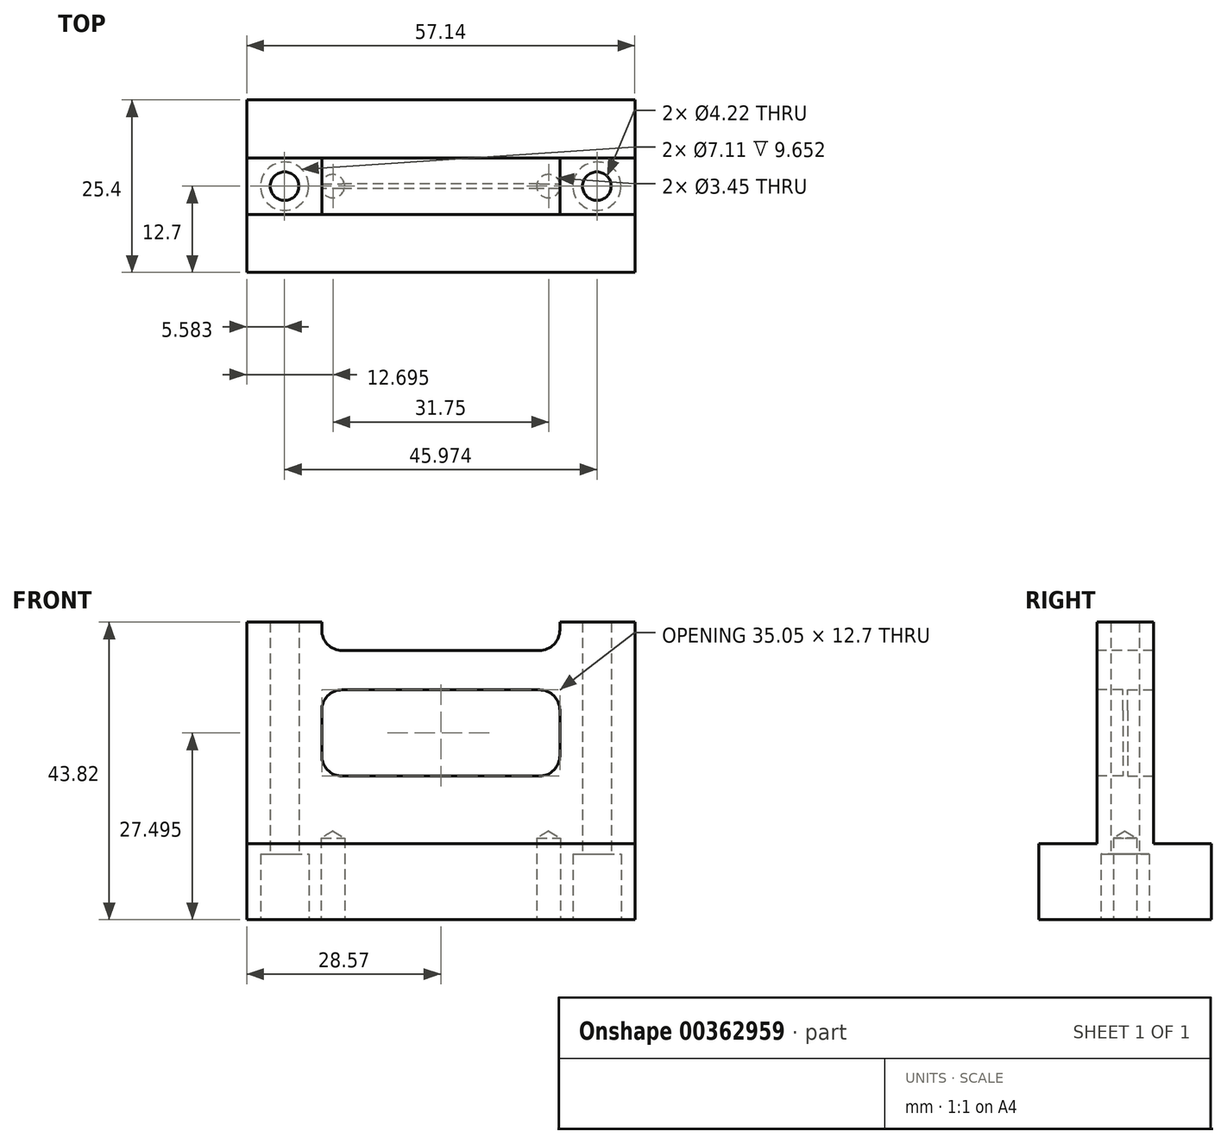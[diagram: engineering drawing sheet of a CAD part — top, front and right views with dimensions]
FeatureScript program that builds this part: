
annotation { "Feature Type Name" : "Feature", "Feature Type Description" : "" }
export const myFeature = defineFeature(function(context is Context, id is Id, definition is map)
    precondition{}
    {
        {
            var Q0;
            Q0=qCreatedBy(makeId("Top.planeOp"),FACE);
            var sketch = newSketch(context, id + "F0", { "sketchPlane" : qUnion([Q0])});
            skLineSegment(sketch, "E0.bottom", {"start": v(28.58, 12.7) * mm, "end": v(-28.58, 12.7) * mm});
            skLineSegment(sketch, "E0.top", {"start": v(28.58, -12.7) * mm, "end": v(-28.58, -12.7) * mm});
            skLineSegment(sketch, "E0.left", {"start": v(28.58, 12.7) * mm, "end": v(28.58, -12.7) * mm});
            skLineSegment(sketch, "E0.right", {"start": v(-28.58, 12.7) * mm, "end": v(-28.58, -12.7) * mm});
            skPoint(sketch, "E0.middle", {"position": v(0, 0) * mm});
            skSolve(sketch);
        }
        {
            var Q0;
            Q0=makeQuery(id+"F0.imprint","IMPRINT",FACE,{"disambiguationData":[TD([[makeQuery(id+"F0.imprint","IMPRINT",EDGE,{"derivedFrom":sQuery(id+"F0.wireOp",EDGE,"E0.bottom")}),1.0]])]});
            extrude(context, id + "F1", {"entities" : qUnion([Q0]), "depth" : 11.18 * mm});
        }
        {
            var Q0;
            Q0=makeQuery(id+"F1.opExtrude","CAP_FACE",FACE,{"disambiguationData":[OSD([sQuery(id+"F0.wireOp",EDGE,"E0.bottom"),sQuery(id+"F0.wireOp",EDGE,"E0.top"),sQuery(id+"F0.wireOp",EDGE,"E0.left"),sQuery(id+"F0.wireOp",EDGE,"E0.right")])],"isStart":false});
            var sketch = newSketch(context, id + "F2", { "sketchPlane" : qUnion([Q0])});
            skLineSegment(sketch, "E1.bottom", {"start": v(28.58, 4.15) * mm, "end": v(-28.58, 4.15) * mm});
            skLineSegment(sketch, "E1.top", {"start": v(28.58, -4.15) * mm, "end": v(-28.58, -4.15) * mm});
            skLineSegment(sketch, "E1.left", {"start": v(28.58, 4.15) * mm, "end": v(28.58, -4.15) * mm});
            skLineSegment(sketch, "E1.right", {"start": v(-28.58, 4.15) * mm, "end": v(-28.58, -4.15) * mm});
            skPoint(sketch, "E1.middle", {"position": v(0, 0) * mm});
            skSolve(sketch);
        }
        {
            var Q0;
            Q0=makeQuery(id+"F2.imprint","IMPRINT",FACE,{"disambiguationData":[TD([[makeQuery(id+"F2.imprint","IMPRINT",EDGE,{"derivedFrom":sQuery(id+"F2.wireOp",EDGE,"E1.bottom")}),1.0]])]});
            extrude(context, id + "F3", {"entities" : qUnion([Q0]), "operationType" : NewBodyOperationType.ADD, "depth" : 32.64 * mm});
        }
        {
            var Q0;
            Q0=makeQuery(id+"F3.opExtrude","SWEPT_FACE",FACE,{"disambiguationData":[OSD([sQuery(id+"F2.wireOp",EDGE,"E1.top")])]});
            var sketch = newSketch(context, id + "F4", { "sketchPlane" : qUnion([Q0])});
            skLineSegment(sketch, "E2.bottom", {"start": v(14.5, 33.85) * mm, "end": v(-14.5, 33.85) * mm});
            skLineSegment(sketch, "E2.top", {"start": v(14.5, 21.15) * mm, "end": v(-14.5, 21.15) * mm});
            skLineSegment(sketch, "E2.left", {"start": v(17.53, 30.82) * mm, "end": v(17.53, 24.17) * mm});
            skLineSegment(sketch, "E2.right", {"start": v(-17.53, 30.82) * mm, "end": v(-17.53, 24.17) * mm});
            skPoint(sketch, "E2.middle", {"position": v(0, 27.5) * mm});
            skPoint(sketch, "E2.middle.positionSnap0", {"position": v(-28.58, 27.5) * mm});
            skPoint(sketch, "E2.middle.positionSnap1", {"position": v(0, 43.82) * mm});
            skPoint(sketch, "E2.centerSnap0", {"position": v(-28.58, 27.5) * mm});
            skPoint(sketch, "E2.centerSnap1", {"position": v(0, 43.82) * mm});
            skPoint(sketch, "E3.visualSharp", {"position": v(-17.53, 33.85) * mm});
            skArc(sketch, "E3.filletArc", {"start": v(-14.5, 33.85) * mm, "mid": v(-16.64, 32.96) * mm, "end": v(-17.53, 30.82) * mm});
            skPoint(sketch, "E4.visualSharp", {"position": v(17.53, 33.85) * mm});
            skArc(sketch, "E4.filletArc", {"start": v(17.53, 30.82) * mm, "mid": v(16.64, 32.96) * mm, "end": v(14.5, 33.85) * mm});
            skPoint(sketch, "E5.visualSharp", {"position": v(17.53, 21.15) * mm});
            skArc(sketch, "E5.filletArc", {"start": v(14.5, 21.15) * mm, "mid": v(16.64, 22.03) * mm, "end": v(17.53, 24.17) * mm});
            skPoint(sketch, "E6.visualSharp", {"position": v(-17.53, 21.15) * mm});
            skArc(sketch, "E6.filletArc", {"start": v(-17.53, 24.17) * mm, "mid": v(-16.64, 22.03) * mm, "end": v(-14.5, 21.15) * mm});
            skLineSegment(sketch, "E7.bottom", {"start": v(-14.5, 39.65) * mm, "end": v(14.5, 39.65) * mm});
            skLineSegment(sketch, "E7.top", {"start": v(-17.53, 47.98) * mm, "end": v(17.53, 47.98) * mm});
            skLineSegment(sketch, "E7.left", {"start": v(-17.53, 42.67) * mm, "end": v(-17.53, 47.98) * mm});
            skLineSegment(sketch, "E7.right", {"start": v(17.53, 42.67) * mm, "end": v(17.53, 47.98) * mm});
            skPoint(sketch, "E8.visualSharp", {"position": v(-17.53, 39.65) * mm});
            skArc(sketch, "E8.filletArc", {"start": v(-17.53, 42.67) * mm, "mid": v(-16.64, 40.54) * mm, "end": v(-14.5, 39.65) * mm});
            skPoint(sketch, "E9.visualSharp", {"position": v(17.53, 39.65) * mm});
            skArc(sketch, "E9.filletArc", {"start": v(14.5, 39.65) * mm, "mid": v(16.64, 40.54) * mm, "end": v(17.53, 42.67) * mm});
            skSolve(sketch);
        }
        {
            var Q0;
            Q0=makeQuery(id+"F4.imprint","IMPRINT",FACE,{"disambiguationData":[TD([[makeQuery(id+"F4.imprint","IMPRINT",EDGE,{"derivedFrom":sQuery(id+"F4.wireOp",EDGE,"E2.bottom")}),1.0]])]});
            extrude(context, id + "F5", {"entities" : qUnion([Q0]), "operationType" : NewBodyOperationType.REMOVE, "oppositeDirection" : true, "depth" : 3.8 * mm});
        }
        {
            var Q0;
            Q0=makeQuery(id+"F4.imprint","IMPRINT",FACE,{"disambiguationData":[TD([[makeQuery(id+"F4.imprint","IMPRINT",EDGE,{"derivedFrom":sQuery(id+"F4.wireOp",EDGE,"E7.bottom")}),1.0]])]});
            extrude(context, id + "F6", {"entities" : qUnion([Q0]), "operationType" : NewBodyOperationType.REMOVE, "endBound" : BoundingType.THROUGH_ALL, "oppositeDirection" : true, "depth" : 25.4 * mm});
        }
        {
            var Q0;
            Q0=makeQuery(id+"F3.opExtrude","SWEPT_FACE",FACE,{"disambiguationData":[OSD([sQuery(id+"F2.wireOp",EDGE,"E1.bottom")])]});
            var sketch = newSketch(context, id + "F7", { "sketchPlane" : qUnion([Q0])});
            skLineSegment(sketch, "E10.0", {"start": v(-17.53, 30.82) * mm, "end": v(-17.53, 24.17) * mm});
            skPoint(sketch, "E11.0", {"position": v(-16.64, 32.96) * mm});
            skLineSegment(sketch, "E12.0", {"start": v(-14.5, 33.85) * mm, "end": v(14.5, 33.85) * mm});
            skLineSegment(sketch, "E13.0", {"start": v(17.53, 30.82) * mm, "end": v(17.53, 24.17) * mm});
            skLineSegment(sketch, "E14.0", {"start": v(-14.5, 21.15) * mm, "end": v(14.5, 21.15) * mm});
            skArc(sketch, "E15.0", {"start": v(17.53, 24.17) * mm, "mid": v(16.64, 22.03) * mm, "end": v(14.5, 21.15) * mm});
            skArc(sketch, "E16.0", {"start": v(14.5, 33.85) * mm, "mid": v(16.64, 32.96) * mm, "end": v(17.53, 30.82) * mm});
            skArc(sketch, "E17.0", {"start": v(-17.53, 30.82) * mm, "mid": v(-16.64, 32.96) * mm, "end": v(-14.5, 33.85) * mm});
            skArc(sketch, "E18.0", {"start": v(-14.5, 21.15) * mm, "mid": v(-16.64, 22.03) * mm, "end": v(-17.53, 24.17) * mm});
            skSolve(sketch);
        }
        {
            var Q0;
            Q0=makeQuery(id+"F7.imprint","IMPRINT",FACE,{"disambiguationData":[TD([[makeQuery(id+"F7.imprint","IMPRINT",EDGE,{"derivedFrom":sQuery(id+"F7.wireOp",EDGE,"E10.0")}),1.0]])]});
            extrude(context, id + "F8", {"entities" : qUnion([Q0]), "operationType" : NewBodyOperationType.REMOVE, "oppositeDirection" : true, "depth" : 3.8 * mm});
        }
        {
            var Q0;
            Q0=makeQuery(id+"F1.opExtrude","CAP_FACE",FACE,{"disambiguationData":[OSD([sQuery(id+"F0.wireOp",EDGE,"E0.bottom"),sQuery(id+"F0.wireOp",EDGE,"E0.top"),sQuery(id+"F0.wireOp",EDGE,"E0.left"),sQuery(id+"F0.wireOp",EDGE,"E0.right")])],"isStart":true});
            var sketch = newSketch(context, id + "F9", { "sketchPlane" : qUnion([Q0])});
            skPoint(sketch, "E19", {"position": v(-22.99, 0) * mm});
            skPoint(sketch, "E20", {"position": v(22.99, 0) * mm});
            skPoint(sketch, "E21", {"position": v(-15.88, 0) * mm});
            skPoint(sketch, "E22", {"position": v(15.88, 0) * mm});
            skSolve(sketch);
        }
        {
            var Q0;
            Q0=sQuery(id+"F9.wireOp",VERTEX,"E19");
            var Q1;
            Q1=sQuery(id+"F9.wireOp",VERTEX,"E20");
            var Q2;
            Q2=makeQuery(id+"F1.opExtrude","SWEPT_BODY",BODY,{"disambiguationData":[OSD([sQuery(id+"F0.wireOp",EDGE,"E0.bottom"),sQuery(id+"F0.wireOp",EDGE,"E0.top"),sQuery(id+"F0.wireOp",EDGE,"E0.left"),sQuery(id+"F0.wireOp",EDGE,"E0.right")])]});
            hole(context, id + "F10", {"style" : HoleStyle.C_BORE, "endStyle" : HoleEndStyle.THROUGH, "holeDiameter" : 4.22 * mm, "cBoreDiameter" : 7.11 * mm, "cBoreDepth" : 9.65 * mm, "isTappedThrough" : true, "tappedDepth" : 12.7 * mm, "tapClearance" : 3, "startFromSketch" : true, "locations" : qUnion([Q0, Q1]), "scope" : qUnion([Q2])});
        }
        {
            var Q0;
            Q0=sQuery(id+"F9.wireOp",VERTEX,"E21");
            var Q1;
            Q1=sQuery(id+"F9.wireOp",VERTEX,"E22");
            var Q2;
            Q2=makeQuery(id+"F1.opExtrude","SWEPT_BODY",BODY,{"disambiguationData":[OSD([sQuery(id+"F0.wireOp",EDGE,"E0.bottom"),sQuery(id+"F0.wireOp",EDGE,"E0.top"),sQuery(id+"F0.wireOp",EDGE,"E0.left"),sQuery(id+"F0.wireOp",EDGE,"E0.right")])]});
            hole(context, id + "F11", {"style" : HoleStyle.SIMPLE, "endStyle" : HoleEndStyle.BLIND, "standardTappedOrClearance" : lookupTablePath({ "standard" : "ANSI", "engagement" : "75%", "pitch" : "32 tpi", "size" : "#8", "type" : "Tapped" }), "standardBlindInLast" : lookupTablePath({ "standard" : "ANSI", "engagement" : "75%", "pitch" : "32 tpi", "size" : "#8", "type" : "Tapped" }), "holeDiameter" : 3.45 * mm, "showTappedDepth" : true, "holeDepth" : 12.03 * mm, "isTappedThrough" : true, "tappedDepth" : 9.65 * mm, "tapClearance" : 3, "startFromSketch" : true, "locations" : qUnion([Q0, Q1]), "scope" : qUnion([Q2]), "majorDiameter" : 4.17 * mm});
        }
    });
